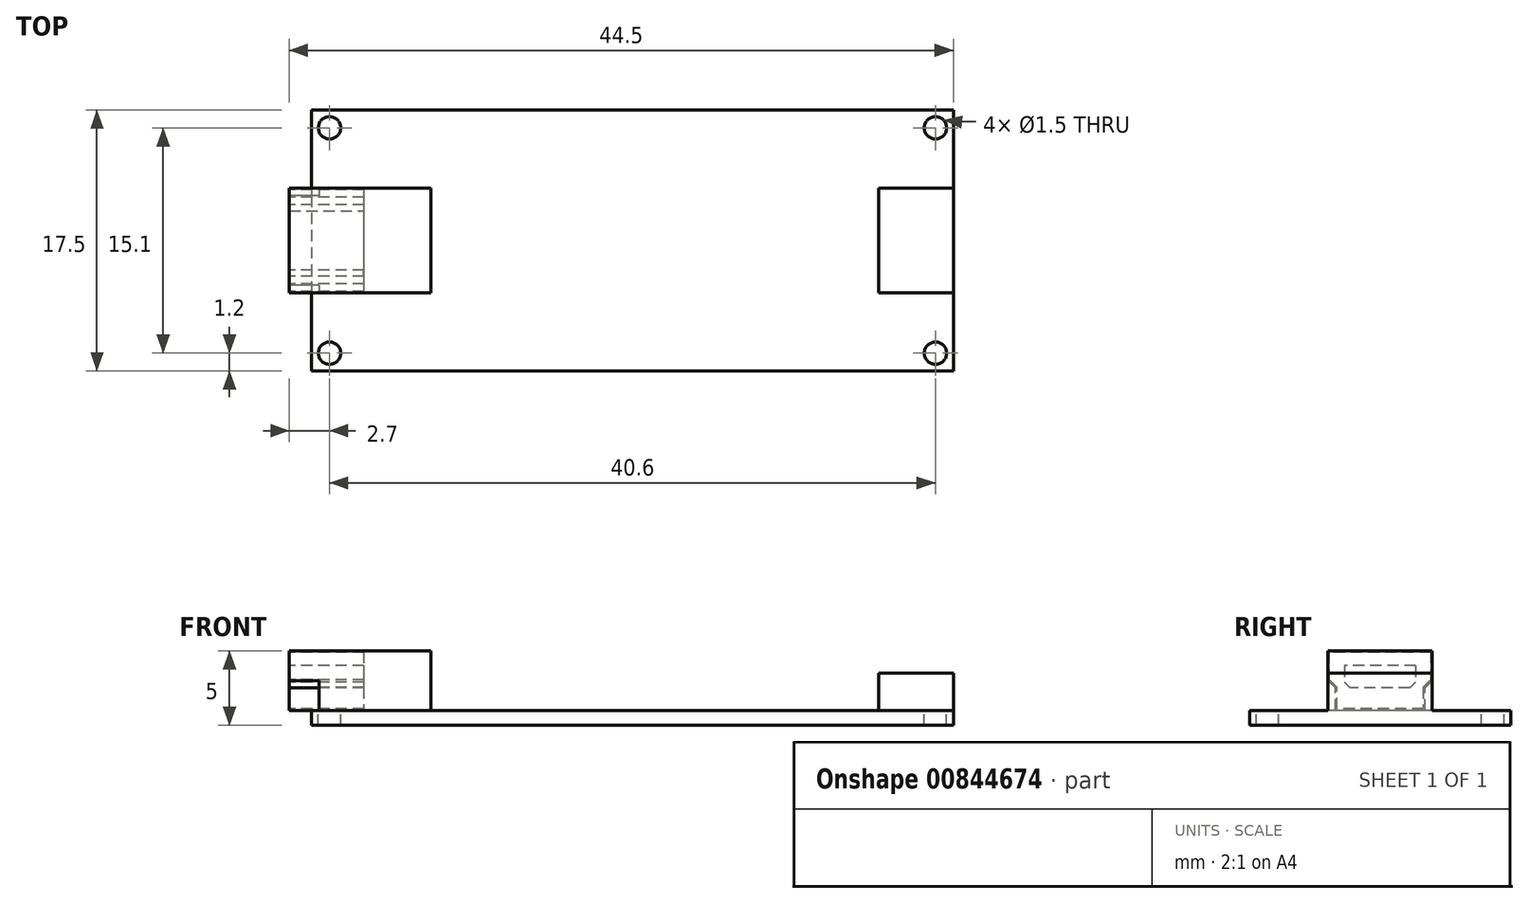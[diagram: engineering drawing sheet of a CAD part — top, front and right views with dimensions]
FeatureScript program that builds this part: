
annotation { "Feature Type Name" : "Feature", "Feature Type Description" : "" }
export const myFeature = defineFeature(function(context is Context, id is Id, definition is map)
    precondition{}
    {
        {
            var Q0;
            Q0=qCreatedBy(makeId("Top.planeOp"),FACE);
            var sketch = newSketch(context, id + "F0", { "sketchPlane" : qUnion([Q0])});
            skLineSegment(sketch, "E0.bottom", {"start": v(21.5, 8.75) * mm, "end": v(-21.5, 8.75) * mm});
            skLineSegment(sketch, "E0.top", {"start": v(21.5, -8.75) * mm, "end": v(-21.5, -8.75) * mm});
            skLineSegment(sketch, "E0.left", {"start": v(21.5, 8.75) * mm, "end": v(21.5, -8.75) * mm});
            skLineSegment(sketch, "E0.right", {"start": v(-21.5, 8.75) * mm, "end": v(-21.5, -8.75) * mm});
            skPoint(sketch, "E0.middle", {"position": v(0, 0) * mm});
            skCircle(sketch, "E1", {"center": v(-20.3, 7.55) * mm, "radius": 0.75 * mm});
            skCircle(sketch, "E2.0.1.0", {"center": v(-20.3, -7.55) * mm, "radius": 0.75 * mm});
            skCircle(sketch, "E2.1.0.0", {"center": v(20.3, 7.55) * mm, "radius": 0.75 * mm});
            skCircle(sketch, "E2.1.1.0", {"center": v(20.3, -7.55) * mm, "radius": 0.75 * mm});
            skLineSegment(sketch, "E2.direction1", {"start": v(-20.3, 7.55) * mm, "end": v(20.3, 7.55) * mm, "construction": true});
            skLineSegment(sketch, "E2.direction2", {"start": v(-20.3, 7.55) * mm, "end": v(-20.3, -7.55) * mm, "construction": true});
            skPoint(sketch, "E3", {"position": v(21.5, 0) * mm});
            skPoint(sketch, "E4", {"position": v(-21.5, 0) * mm});
            skLineSegment(sketch, "E5.bottom", {"start": v(-23, 3.5) * mm, "end": v(-13.5, 3.5) * mm});
            skLineSegment(sketch, "E5.top", {"start": v(-23, -3.5) * mm, "end": v(-13.5, -3.5) * mm});
            skLineSegment(sketch, "E5.left", {"start": v(-23, 3.5) * mm, "end": v(-23, -3.5) * mm});
            skLineSegment(sketch, "E5.right", {"start": v(-13.5, 3.5) * mm, "end": v(-13.5, -3.5) * mm});
            skPoint(sketch, "E6", {"position": v(-13.5, 0) * mm});
            skLineSegment(sketch, "E7.bottom", {"start": v(21.5, 3.5) * mm, "end": v(16.5, 3.5) * mm});
            skLineSegment(sketch, "E7.top", {"start": v(21.5, -3.5) * mm, "end": v(16.5, -3.5) * mm});
            skLineSegment(sketch, "E7.left", {"start": v(21.5, 3.5) * mm, "end": v(21.5, -3.5) * mm});
            skLineSegment(sketch, "E7.right", {"start": v(16.5, 3.5) * mm, "end": v(16.5, -3.5) * mm});
            skSolve(sketch);
        }
        {
            var Q0;
            {var subQ5=sQuery(id+"F0.wireOp",EDGE,"E5.right");Q0=makeQuery(id+"F0.imprint","IMPRINT",FACE,{"disambiguationData":[TD([[makeQuery(id+"F0.imprint","IMPRINT",EDGE,{"derivedFrom":subQ5}),-1.0]])]});}
            var Q1;
            {var subQ0=sQuery(id+"F0.wireOp",EDGE,"E0.bottom");Q1=makeQuery(id+"F0.imprint","IMPRINT",FACE,{"disambiguationData":[TD([[makeQuery(id+"F0.imprint","IMPRINT",EDGE,{"derivedFrom":subQ0}),1.0]])]});}
            var Q2;
            Q2=makeQuery(id+"F0.imprint","IMPRINT",FACE,{"disambiguationData":[TD([[makeQuery(id+"F0.imprint","IMPRINT",EDGE,{"derivedFrom":sQuery(id+"F0.wireOp",EDGE,"E7.bottom")}),1.0]])]});
            extrude(context, id + "F1", {"entities" : qUnion([Q0, Q1, Q2]), "oppositeDirection" : true, "depth" : 1 * mm});
        }
        {
            var Q0;
            {var subQ5=sQuery(id+"F0.wireOp",EDGE,"E5.left");Q0=makeQuery(id+"F0.imprint","IMPRINT",FACE,{"disambiguationData":[TD([[makeQuery(id+"F0.imprint","IMPRINT",EDGE,{"derivedFrom":subQ5}),1.0]])]});}
            var Q1;
            {var subQ5=sQuery(id+"F0.wireOp",EDGE,"E5.right");Q1=makeQuery(id+"F0.imprint","IMPRINT",FACE,{"disambiguationData":[TD([[makeQuery(id+"F0.imprint","IMPRINT",EDGE,{"derivedFrom":subQ5}),-1.0]])]});}
            extrude(context, id + "F2", {"entities" : qUnion([Q0, Q1]), "operationType" : NewBodyOperationType.ADD, "depth" : 4 * mm});
        }
        {
            var Q0;
            Q0=makeQuery(id+"F0.imprint","IMPRINT",FACE,{"disambiguationData":[TD([[makeQuery(id+"F0.imprint","IMPRINT",EDGE,{"derivedFrom":sQuery(id+"F0.wireOp",EDGE,"E7.bottom")}),1.0]])]});
            extrude(context, id + "F3", {"entities" : qUnion([Q0]), "operationType" : NewBodyOperationType.ADD, "depth" : 2.5 * mm});
        }
        {
            var Q0;
            Q0=makeQuery(id+"F2.opExtrude","SWEPT_FACE",FACE,{"disambiguationData":[OSD([sQuery(id+"F0.wireOp",EDGE,"E5.left")])]});
            var sketch = newSketch(context, id + "F4", { "sketchPlane" : qUnion([Q0])});
            skPoint(sketch, "E8", {"position": v(-3.5, 2) * mm});
            skPoint(sketch, "E9", {"position": v(3.5, 2) * mm});
            skPoint(sketch, "E10", {"position": v(-3, 0) * mm});
            skPoint(sketch, "E11", {"position": v(3, 0) * mm});
            skPoint(sketch, "E12", {"position": v(-3, 1.5) * mm});
            skPoint(sketch, "E13", {"position": v(3, 1.5) * mm});
            skLineSegment(sketch, "E14", {"start": v(-3.5, 2) * mm, "end": v(-3, 1.5) * mm});
            skLineSegment(sketch, "E15", {"start": v(-3, 0) * mm, "end": v(-3, 1.5) * mm});
            skLineSegment(sketch, "E16", {"start": v(3, 0) * mm, "end": v(3, 1.5) * mm});
            skLineSegment(sketch, "E17", {"start": v(3, 1.5) * mm, "end": v(3.5, 2) * mm});
            skLineSegment(sketch, "E18.bottom", {"start": v(-2.4, 3) * mm, "end": v(2.4, 3) * mm});
            skLineSegment(sketch, "E18.top", {"start": v(-2.4, 1.5) * mm, "end": v(2.4, 1.5) * mm});
            skLineSegment(sketch, "E18.left", {"start": v(-2.4, 3) * mm, "end": v(-2.4, 1.5) * mm});
            skLineSegment(sketch, "E18.right", {"start": v(2.4, 3) * mm, "end": v(2.4, 1.5) * mm});
            skPoint(sketch, "E19", {"position": v(0, 3) * mm});
            skPoint(sketch, "E20", {"position": v(-2.4, 2.25) * mm});
            skPoint(sketch, "E21", {"position": v(-3.5, 4) * mm});
            skPoint(sketch, "E22", {"position": v(3.5, 4) * mm});
            skLineSegment(sketch, "E23.0", {"start": v(-3.5, -1) * mm, "end": v(3.5, -1) * mm});
            skLineSegment(sketch, "E24", {"start": v(-3.5, 4) * mm, "end": v(-3.5, 2) * mm});
            skLineSegment(sketch, "E25", {"start": v(-3, 1.5) * mm, "end": v(-3, 0) * mm});
            skLineSegment(sketch, "E26", {"start": v(-3, 0) * mm, "end": v(3, 0) * mm});
            skLineSegment(sketch, "E27", {"start": v(3.5, 2) * mm, "end": v(3.5, 4) * mm});
            skLineSegment(sketch, "E28.0", {"start": v(-3.4, 3.9) * mm, "end": v(3.4, 3.9) * mm});
            skLineSegment(sketch, "E28.1", {"start": v(3.4, 2.04) * mm, "end": v(3.4, 3.9) * mm});
            skLineSegment(sketch, "E28.2", {"start": v(-3.4, 3.9) * mm, "end": v(-3.4, 2.04) * mm});
            skLineSegment(sketch, "E28.3", {"start": v(2.9, 1.54) * mm, "end": v(3.4, 2.04) * mm});
            skLineSegment(sketch, "E28.4", {"start": v(-3.4, 2.04) * mm, "end": v(-2.9, 1.54) * mm});
            skLineSegment(sketch, "E28.5", {"start": v(-2.9, 1.54) * mm, "end": v(-2.9, 0.1) * mm});
            skLineSegment(sketch, "E28.6", {"start": v(-2.9, 0.1) * mm, "end": v(2.9, 0.1) * mm});
            skLineSegment(sketch, "E28.7", {"start": v(2.9, 0.1) * mm, "end": v(2.9, 1.54) * mm});
            skPoint(sketch, "E29", {"position": v(-3.4, 2.04) * mm});
            skPoint(sketch, "E30", {"position": v(-2.9, 1.54) * mm});
            skSolve(sketch);
        }
        {
            var Q0;
            Q0=makeQuery(id+"F4.imprint","IMPRINT",FACE,{"disambiguationData":[TD([[makeQuery(id+"F4.imprint","IMPRINT",EDGE,{"derivedFrom":sQuery(id+"F4.wireOp",EDGE,"E18.bottom")}),1.0]])]});
            extrude(context, id + "F5", {"entities" : qUnion([Q0]), "operationType" : NewBodyOperationType.REMOVE, "oppositeDirection" : true, "depth" : 5 * mm});
        }
        {
            var Q0;
            {var subQ0=sQuery(id+"F4.wireOp",EDGE,"E14");Q0=makeQuery(id+"F4.imprint","IMPRINT",FACE,{"disambiguationData":[TD([[makeQuery(id+"F4.imprint","IMPRINT",EDGE,{"derivedFrom":subQ0}),-1.0]])]});}
            var Q1;
            {var subQ0=sQuery(id+"F4.wireOp",EDGE,"E16");Q1=makeQuery(id+"F4.imprint","IMPRINT",FACE,{"disambiguationData":[TD([[makeQuery(id+"F4.imprint","IMPRINT",EDGE,{"derivedFrom":subQ0}),-1.0]])]});}
            extrude(context, id + "F6", {"entities" : qUnion([Q0, Q1]), "operationType" : NewBodyOperationType.REMOVE, "oppositeDirection" : true, "depth" : 2 * mm});
        }
        {
            var Q0;
            Q0=makeQuery(id+"F5.boolean.opBoolean","COPY",EDGE,{"derivedFrom":makeQuery(id+"F5.opExtrude","SWEPT_EDGE",EDGE,{"disambiguationData":[OSD([sQuery(id+"F4.wireOp",EDGE,"E18.top"),sQuery(id+"F4.wireOp",EDGE,"E18.right")])]})});
            var Q1;
            Q1=makeQuery(id+"F5.boolean.opBoolean","COPY",EDGE,{"derivedFrom":makeQuery(id+"F5.opExtrude","SWEPT_EDGE",EDGE,{"disambiguationData":[OSD([sQuery(id+"F4.wireOp",EDGE,"E18.top"),sQuery(id+"F4.wireOp",EDGE,"E18.left")])]})});
            chamfer(context, id + "F7", {"entities" : qUnion([Q0, Q1]), "width" : 0.4 * mm, "tangentPropagation" : true});
        }
    });
